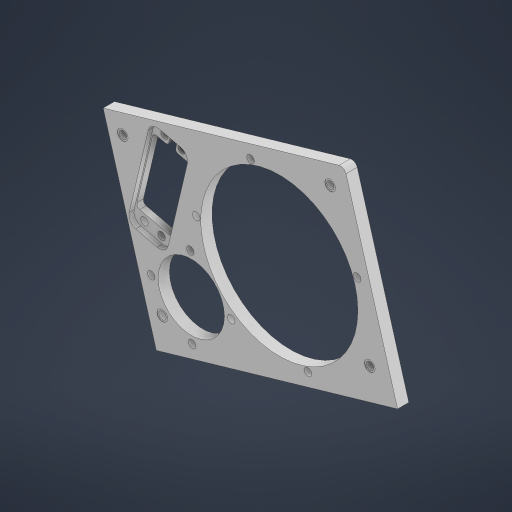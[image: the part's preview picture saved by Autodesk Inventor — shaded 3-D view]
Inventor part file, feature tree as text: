
AUTODESK INVENTOR PART (.ipt)
format: ipt  version: 2024.2 (Build 282272000, 272)  size: 374,272 bytes
history: native  units: in
note: dims shown in document units (in); Inventor stores cm internally (conversion verified against a paired STEP export)
features: reference x20, other x8, extrude x5, sketch x5, fillet x2
ambient origin geometry x8: Origin, YZ Plane, XZ Plane, XY Plane, X Axis, Y Axis, Z Axis, Center Point
bodies: Solid1 (feature_tree)
feature tree (40):
  extrude  "Extrusion1"  Depth=0.1693in
  extrude  "Extrusion2"  Depth=0.1693in
  extrude  "Extrusion3"  TaperAngle=0.0deg  [1 undecoded]
  fillet  "Fillet1"  Radius=0.1969in
  fillet  "Fillet2"  Radius=0.1969in
  extrude  "Extrusion4"  Depth=0.1969in
  extrude  "Extrusion5"  Depth=0.25in TaperAngle=0.0deg
  sketch  "Sketch1"  dims[d4=0.1693in d5=0.1693in]
  reference  "Reference1"
  reference  "Reference2"
  reference  "Reference4"
  reference  "Reference9"
  reference  "Reference10"
  reference  "Reference11"
  reference  "Reference12"
  reference  "Reference13"
  reference  "Reference14"
  sketch  "Sketch3"  dims[d6=0.1693in d7=0.1693in]
  sketch  "Sketch4"  dims[d8=0.1969in d10=0.0in d11=0.1969in d12=0.1969in]
  reference  "Reference15"
  reference  "Reference16"
  reference  "Reference17"
  sketch  "Sketch5"  dims[d13=0.0in d14=0.1969in]
  reference  "Reference18"
  reference  "Reference19"
  reference  "Reference20"
  reference  "Reference21"
  sketch  "Sketch6"  dims[d15=0.1969in d16=0.25in d17=0.0in d18=0.2697in d19=0.0in d20=0.0in d21=0.1073in d22=0.0in d23=0.05in d24=0.05in d25=0.3787in d26=0.8453in d27=0.3197in d28=0.2in d29=0.1693in d30=0.1693in d31=0.1693in d32=0.1693in d33=0.2362in d34=0.2362in d35=0.05in d36=0.0in d37=0.0in d38=0.0in d39=0.025in d40=0.0625in d41=0.025in d42=0.125in d43=0.2402in d44=0.2402in d45=0.2402in d46=0.2402in d47=0.0059in d48=0.0in d49=0.0in d50=0.0in]
  reference  "Reference22"
  reference  "Reference23"
  reference  "Reference24"
  reference  "Reference25"
  other  "<userpath>\Desktop\Robotics\Swerve2\Assemblies\Pod.iam"
  other  "Pod.iam"
  other  "big_funny_washer:1"
  other  "5000-0002-0001 assembly_1"
  other  "5000-0002-0001 motor shield_13"
  other  "Axon_MINI:1"
  parser-record x1  (decoder bookkeeping rows leaked as tree rows — omitted from the tree; the rows remain in map.json)
  other  "Upper_Plate:1"
note: 1 required parameter value undecoded (feature->parameter linkage not recoverable at this tier; creation-order binding heuristic only, values carry confidence <= 0.55)
